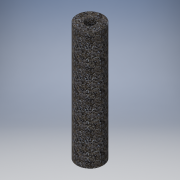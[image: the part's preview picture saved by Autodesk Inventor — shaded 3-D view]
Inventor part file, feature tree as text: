
AUTODESK INVENTOR PART (.ipt)
format: ipt  version: 2019 (Build 230136000, 136)  size: 110,080 bytes
history: native  units: in
note: dims shown in document units (in); Inventor stores cm internally (conversion verified against a paired STEP export)
features: extrude x1, sketch x1
ambient origin geometry x8: Origin, YZ Plane, XZ Plane, XY Plane, X Axis, Y Axis, Z Axis, Center Point
bodies: Solid1 (feature_tree)
feature tree (2):
  extrude  "Extrusion1"  Depth=39.3701in
  sketch  "Sketch1"  dims[d0=3.1496in d1=8.6614in d2=39.3701in d3=0.0in]
